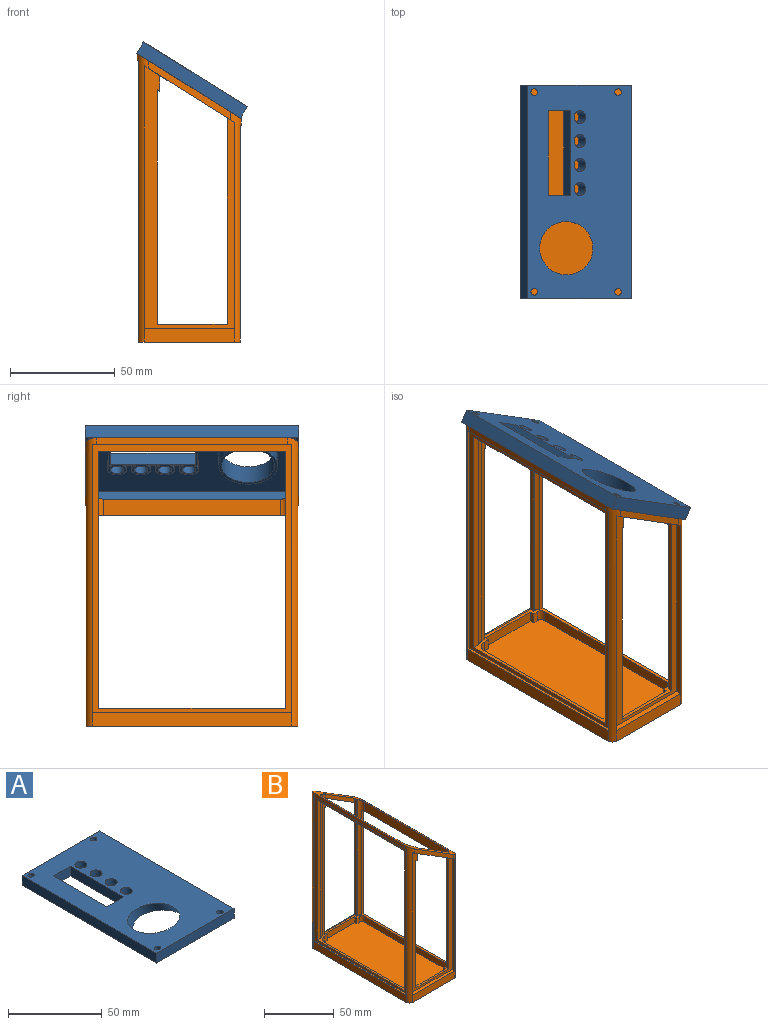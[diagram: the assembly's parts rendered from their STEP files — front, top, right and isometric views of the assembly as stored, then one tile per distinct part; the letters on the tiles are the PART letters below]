
ASSEMBLY  parts=2 mates=1
PART A: 49 faces, bbox 58.4x101.6x34.8 mm
  f0: plane 43.18x23.41mm, normal (0,0,-1), area 253.1mm2, adj f13,f14,f15,f16,f17,f18,f19,f20
  f1: plane 101.6x58.42mm, normal (0,0,-1), area 463.9mm2, adj f3,f4,f5,f6,f9,f10,f11,f12
  f2: plane 32.95x27.94mm, normal (0,0,-1), area 125.5mm2, adj f8,f36
  f3: plane 101.6x6.35mm, normal (1,0,0), area 645.2mm2, adj f1,f4,f6,f7
  f4: plane 58.42x6.35mm, normal (0,-1,0), area 371mm2, adj f1,f3,f5,f7
  f5: plane 101.6x6.35mm, normal (-1,0,0), area 645.2mm2, adj f1,f4,f6,f7
  f6: plane 58.42x6.35mm, normal (0,1,0), area 371mm2, adj f1,f3,f5,f7
  f7: plane 101.6x58.42mm, normal (0,0,1), area 4662.7mm2, adj f3,f4,f5,f6,f8,f9,f10,f11
  f8: cylinder r=12.7mm len=33.98mm, axis (-0.53,0,0.85), area 597.5mm2, adj f2,f7
  f9: cylinder r=1.59mm len=9.73mm, axis (-0.53,0,0.85), area 74.7mm2, adj f1,f7
  f10: cylinder r=1.59mm len=9.73mm, axis (-0.53,0,0.85), area 74.7mm2, adj f1,f7
  f11: cylinder r=1.59mm len=9.73mm, axis (-0.53,0,0.85), area 74.7mm2, adj f1,f7
  f12: cylinder r=1.59mm len=9.73mm, axis (-0.53,0,0.85), area 74.7mm2, adj f1,f7
  f13: plane 40.26x6.35mm, normal (1,0,0), area 255.6mm2, adj f0,f7,f14,f16
  f14: plane 12.7x6.35mm, normal (0,-1,0), area 80.6mm2, adj f0,f7,f13,f15
  f15: plane 40.26x6.35mm, normal (-1,0,0), area 255.6mm2, adj f0,f7,f14,f16
  f16: plane 12.7x6.35mm, normal (0,1,0), area 80.6mm2, adj f0,f7,f13,f15
  f17: cylinder r=3.17mm len=6.35mm, axis (0,0,1), area 126.7mm2, adj f0,f7
  f18: cylinder r=3.17mm len=6.35mm, axis (0,0,1), area 126.7mm2, adj f0,f7
  f19: cylinder r=3.17mm len=6.35mm, axis (0,0,1), area 126.7mm2, adj f0,f7
  f20: cylinder r=3.17mm len=6.35mm, axis (0,0,1), area 126.7mm2, adj f0,f7
  f21: plane 5.08x1.83mm, normal (1,0,0), area 9.3mm2, adj f0,f35,f42,f48
  f22: plane 6.58x5.08mm, normal (1,0,0), area 33.4mm2, adj f0,f35,f47,f48
  f23: plane 6.58x5.08mm, normal (1,0,0), area 33.4mm2, adj f0,f35,f46,f47
  f24: plane 6.58x5.08mm, normal (1,0,0), area 33.4mm2, adj f0,f35,f45,f46
  f25: plane 4.66x2.91mm, normal (0,-1,0), area 6.8mm2, adj f31,f35,f40
  f26: plane 4.66x2.91mm, normal (0,1,0), area 6.8mm2, adj f31,f35,f39
  f27: plane 45.34x5.08mm, normal (0,1,0), area 214.2mm2, adj f1,f35,f38,f39
  f28: plane 45.34x5.08mm, normal (0,-1,0), area 214.2mm2, adj f1,f35,f37,f40
  f29: plane 1.21x0.76mm, normal (0,0,-1), area 0.4mm2, adj f32,f33,f38
  f30: plane 1.21x0.76mm, normal (0,0,-1), area 0.4mm2, adj f33,f34,f37
  f31: plane 99.06x5.08mm, normal (-1,0,0), area 492.8mm2, adj f1,f25,f26,f35,f39,f40
  f32: plane 5.08x3.93mm, normal (0,1,0), area 11.9mm2, adj f1,f29,f33,f38
  f33: plane 99.06x5.08mm, normal (1,0,0), area 502.9mm2, adj f1,f29,f30,f32,f34,f35,f37,f38
  f34: plane 5.08x3.93mm, normal (0,-1,0), area 11.9mm2, adj f1,f30,f33,f37
  f35: plane 99.06x55.88mm, normal (0,0,-1), area 3813.2mm2, adj f21,f22,f23,f24,f25,f26,f27,f28
  f36: cylinder r=13.97mm len=36.19mm, axis (-0.53,0,0.85), area 525.8mm2, adj f2,f35
  f37: cylinder r=2.86mm len=11.09mm, axis (-0.53,0,0.85), area 78.6mm2, adj f1,f28,f30,f33,f34,f35
  f38: cylinder r=2.86mm len=11.09mm, axis (-0.53,0,0.85), area 78.6mm2, adj f1,f27,f29,f32,f33,f35
  f39: cylinder r=2.86mm len=10.64mm, axis (-0.53,0,0.85), area 72.2mm2, adj f1,f26,f27,f31,f35
  f40: cylinder r=2.86mm len=10.64mm, axis (-0.53,0,0.85), area 72.2mm2, adj f1,f25,f28,f31,f35
  f41: plane 42.8x5.08mm, normal (-1,0,0), area 217.4mm2, adj f0,f35,f42,f44
  f42: plane 15.24x5.08mm, normal (0,1,0), area 77.4mm2, adj f0,f21,f35,f41
  f43: plane 5.08x1.83mm, normal (1,0,0), area 9.3mm2, adj f0,f35,f44,f45
  f44: plane 15.24x5.08mm, normal (0,-1,0), area 77.4mm2, adj f0,f35,f41,f43
  f45: cylinder r=4.45mm len=8.89mm, axis (0,0,1), area 115.8mm2, adj f0,f24,f35,f43
  f46: cylinder r=4.45mm len=8.89mm, axis (0,0,1), area 115.8mm2, adj f0,f23,f24,f35
  f47: cylinder r=4.45mm len=8.89mm, axis (0,0,1), area 115.8mm2, adj f0,f22,f23,f35
  f48: cylinder r=4.45mm len=8.89mm, axis (0,0,1), area 115.8mm2, adj f0,f21,f22,f35
PART B: 78 faces, bbox 49.5x101.6x137.5 mm
  f0: plane 95.25x1.22mm, normal (0,0,1), area 115.9mm2, adj f42,f44,f45,f58
  f1: plane 43.19x2.8mm, normal (0,0,1), area 121.1mm2, adj f23,f24,f25,f55
  f2: plane 95.25x1.22mm, normal (0,0,1), area 115.9mm2, adj f38,f40,f41,f56
  f3: plane 91.44x3.18mm, normal (1,0,0), area 290.3mm2, adj f32,f43,f48,f50
  f4: plane 88.9x3.14mm, normal (0,0,-1), area 103.2mm2, adj f5,f6,f17,f41,f46,f47
  f5: plane 122.78x3.14mm, normal (0,1,0), area 385.7mm2, adj f4,f41,f46,f72
  f6: plane 122.78x3.14mm, normal (0,-1,0), area 385.7mm2, adj f4,f41,f47,f72
  f7: plane 84.58x8.03mm, normal (-1,0,0), area 679.4mm2, adj f32,f35,f52,f53
  f8: plane 91.44x3.18mm, normal (-1,0,0), area 290.3mm2, adj f32,f39,f49,f51
  f9: plane 39.38x28.35mm, normal (0,1,0), area 147.4mm2, adj f32,f34,f48,f49
  f10: plane 111.95x2.16mm, normal (1,0,0), area 242.1mm2, adj f13,f23,f26,f72
  f11: plane 39.38x28.35mm, normal (0,-1,0), area 147.4mm2, adj f32,f33,f50,f51
  f12: plane 111.95x2.16mm, normal (1,0,0), area 242.1mm2, adj f14,f20,f28,f72
  f13: plane 124.27x3mm, normal (0,-1,0), area 230.8mm2, adj f10,f26,f30,f32,f47,f72
  f14: plane 124.27x3mm, normal (0,1,0), area 230.8mm2, adj f12,f28,f31,f32,f46,f72
  f15: plane 102.38x0.86mm, normal (0,-1,0), area 88.2mm2, adj f16,f32,f53,f72
  f16: plane 102.38x2.16mm, normal (-1,0,0), area 221.4mm2, adj f15,f23,f29,f32,f72
  f17: plane 80.77x4.67mm, normal (1,0,0), area 377mm2, adj f4,f32,f46,f47
  f18: plane 102.38x2.16mm, normal (-1,0,0), area 221.4mm2, adj f19,f20,f27,f32,f72
  f19: plane 102.38x0.86mm, normal (0,1,0), area 88.2mm2, adj f18,f32,f52,f72
  f20: plane 125.44x43.19mm, normal (0,-1,0), area 1215.1mm2, adj f12,f18,f21,f22,f28,f31,f33,f54
  f21: plane 125.44x2.8mm, normal (1,0,0), area 351.8mm2, adj f20,f33,f51,f54
  f22: plane 98.45x2.8mm, normal (-1,0,0), area 276.1mm2, adj f20,f33,f50,f54
  f23: plane 125.44x43.19mm, normal (0,1,0), area 1215.1mm2, adj f1,f10,f16,f24,f25,f26,f30,f34
  f24: plane 98.45x2.8mm, normal (-1,0,0), area 276.1mm2, adj f1,f23,f34,f48
  f25: plane 125.44x2.8mm, normal (1,0,0), area 351.8mm2, adj f1,f23,f34,f49
  f26: plane 2.16x1.25mm, normal (-0.53,0,-0.85), area 3.2mm2, adj f10,f13,f23,f30
  f27: plane 32.04x23.77mm, normal (0,1,0), area 120mm2, adj f18,f31,f32,f33
  f28: plane 2.16x1.25mm, normal (-0.53,0,-0.85), area 3.2mm2, adj f12,f14,f20,f31
  f29: plane 32.04x23.77mm, normal (0,-1,0), area 120mm2, adj f16,f30,f32,f34
  f30: plane 11.23x2.16mm, normal (1,0,0), area 24.3mm2, adj f13,f23,f26,f29,f32
  f31: plane 11.23x2.16mm, normal (1,0,0), area 24.3mm2, adj f14,f20,f27,f28,f32
  f32: plane 101.6x49.54mm, normal (0.53,0,0.85), area 1029.6mm2, adj f3,f7,f8,f9,f11,f13,f14,f15
  f33: plane 43.19x26.99mm, normal (-0.53,0,-0.85), area 161.2mm2, adj f11,f20,f21,f22,f27,f50,f51
  f34: plane 43.19x26.99mm, normal (-0.53,0,-0.85), area 161.2mm2, adj f9,f23,f24,f25,f29,f48,f49
  f35: plane 88.9x1.96mm, normal (0,0,-1), area 99.4mm2, adj f7,f36,f37,f45,f52,f53
  f36: plane 91.82x1.96mm, normal (0,-1,0), area 179.5mm2, adj f35,f45,f53,f72
  f37: plane 91.82x1.96mm, normal (0,1,0), area 179.5mm2, adj f35,f45,f52,f72
  f38: plane 127.99x1.22mm, normal (0,1,0), area 155.7mm2, adj f2,f39,f41,f51
  f39: plane 95.25x1.59mm, normal (0,0,-1), area 150.7mm2, adj f8,f38,f40,f41,f49,f51
  f40: plane 127.99x1.22mm, normal (0,-1,0), area 155.7mm2, adj f2,f39,f41,f49
  f41: plane 127.99x95.25mm, normal (-1,0,0), area 1276mm2, adj f2,f4,f5,f6,f38,f39,f40,f72
  f42: plane 97.03x1.22mm, normal (0,-1,0), area 118.1mm2, adj f0,f43,f45,f48
  f43: plane 95.25x1.59mm, normal (0,0,-1), area 150.7mm2, adj f3,f42,f44,f45,f48,f50
  f44: plane 97.03x1.22mm, normal (0,1,0), area 118.1mm2, adj f0,f43,f45,f50
  f45: plane 97.03x95.25mm, normal (1,0,0), area 1079.4mm2, adj f0,f35,f36,f37,f42,f43,f44,f72
  f46: cylinder r=5.08mm len=127.45mm, axis (0,0,-1), area 428.7mm2, adj f4,f5,f14,f17,f32,f72
  f47: cylinder r=5.08mm len=127.45mm, axis (0,0,-1), area 428.7mm2, adj f4,f6,f13,f17,f32,f72
  f48: cylinder r=5.08mm len=109.73mm, axis (0,0,1), area 451.8mm2, adj f3,f9,f24,f32,f34,f42,f43,f55
  f49: cylinder r=5.08mm len=137.52mm, axis (0,0,-1), area 569.6mm2, adj f8,f9,f25,f32,f34,f39,f40,f55
  f50: cylinder r=5.08mm len=109.73mm, axis (0,0,-1), area 451.8mm2, adj f3,f11,f22,f32,f33,f43,f44,f57
  f51: cylinder r=5.08mm len=137.52mm, axis (0,0,1), area 569.6mm2, adj f8,f11,f21,f32,f33,f38,f39,f56
  f52: cylinder r=3.17mm len=101.84mm, axis (0,0,-1), area 283.2mm2, adj f7,f19,f32,f35,f37,f72
  f53: cylinder r=3.17mm len=101.84mm, axis (0,0,-1), area 283.2mm2, adj f7,f15,f32,f35,f36,f72
  f54: plane 43.19x2.8mm, normal (0,0,1), area 121.1mm2, adj f20,f21,f22,f57
  f55: plane 43.19x6.35mm, normal (0,1,0), area 274.3mm2, adj f1,f48,f49,f59
  f56: plane 95.25x6.35mm, normal (-1,0,0), area 604.8mm2, adj f2,f49,f51,f59
  f57: plane 43.19x6.35mm, normal (0,-1,0), area 274.3mm2, adj f50,f51,f54,f59
  f58: plane 95.25x6.35mm, normal (1,0,0), area 604.8mm2, adj f0,f48,f50,f59
  f59: plane 100.86x48.8mm, normal (0,0,-1), area 4910.6mm2, adj f48,f49,f50,f51,f55,f56,f57,f58
  f60: plane 5.21x2.16mm, normal (-1,0,0), area 11.3mm2, adj f61,f71,f72,f73
  f61: plane 30.11x5.21mm, normal (0,1,0), area 156.9mm2, adj f60,f62,f72,f73
  f62: plane 5.21x2.16mm, normal (1,0,0), area 11.3mm2, adj f61,f63,f72,f73
  f63: plane 5.21x2.86mm, normal (0,1,0), area 14.9mm2, adj f62,f72,f73,f76
  f64: plane 77.59x5.21mm, normal (1,0,0), area 404.3mm2, adj f72,f73,f75,f76
  f65: plane 5.21x2.86mm, normal (0,-1,0), area 14.9mm2, adj f66,f72,f73,f75
  f66: plane 5.21x2.16mm, normal (1,0,0), area 11.3mm2, adj f65,f67,f72,f73
  f67: plane 30.11x5.21mm, normal (0,-1,0), area 156.9mm2, adj f66,f68,f72,f73
  f68: plane 5.21x2.16mm, normal (-1,0,0), area 11.3mm2, adj f67,f69,f72,f73
  f69: plane 5.21x2.6mm, normal (0,-1,0), area 13.6mm2, adj f68,f72,f73,f74
  f70: plane 82.67x5.21mm, normal (-1,0,0), area 430.8mm2, adj f72,f73,f74,f77
  f71: plane 5.21x2.6mm, normal (0,1,0), area 13.6mm2, adj f60,f72,f73,f77
  f72: plane 95.25x46.37mm, normal (0,0,1), area 439.7mm2, adj f5,f6,f10,f12,f13,f14,f15,f16
  f73: plane 92.08x43.19mm, normal (0,0,1), area 3906.6mm2, adj f60,f61,f62,f63,f64,f65,f66,f67
  f74: cylinder r=2.54mm len=5.21mm, axis (0,0,1), area 20.8mm2, adj f69,f70,f72,f73
  f75: cylinder r=5.08mm len=5.21mm, axis (0,0,1), area 41.6mm2, adj f64,f65,f72,f73
  f76: cylinder r=5.08mm len=5.21mm, axis (0,0,1), area 41.6mm2, adj f63,f64,f72,f73
  f77: cylinder r=2.54mm len=5.21mm, axis (0,0,1), area 20.8mm2, adj f70,f71,f72,f73
PLACE A rot(axis=(0,1,0),32deg) t=(55.7,25.1,39.29)mm
PLACE B t=(50.94,75.9,-18.54)mm fixed
MATE fastened A.f0 <-> B.f32  axis (-0.53,0,-0.85) through (52.26,25.1,33.95)mm
